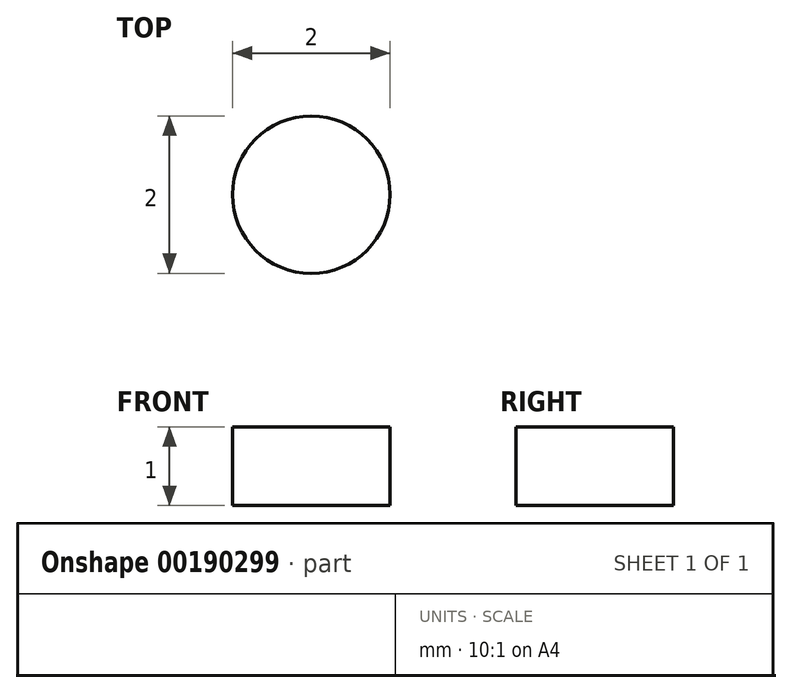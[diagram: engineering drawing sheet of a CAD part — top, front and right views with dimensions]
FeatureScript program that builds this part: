
annotation { "Feature Type Name" : "Feature", "Feature Type Description" : "" }
export const myFeature = defineFeature(function(context is Context, id is Id, definition is map)
    precondition{}
    {
        {
            var Q0;
            Q0=qCreatedBy(makeId("Top.planeOp"),FACE);
            var sketch = newSketch(context, id + "F0", { "sketchPlane" : qUnion([Q0])});
            skCircle(sketch, "E0", {"center": v(0, 0) * mm, "radius": 1 * mm});
            skSolve(sketch);
        }
        {
            var Q0;
            Q0=makeQuery(id+"F0.imprint","IMPRINT",FACE,{"disambiguationData":[TD([[makeQuery(id+"F0.imprint","IMPRINT",EDGE,{"derivedFrom":sQuery(id+"F0.wireOp",EDGE,"E0")}),1.0]])]});
            extrude(context, id + "F1", {"entities" : qUnion([Q0]), "depth" : 1 * mm});
        }
    });
